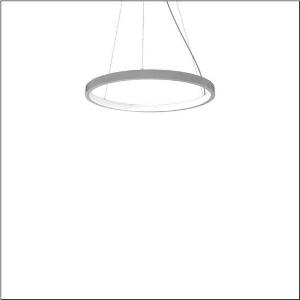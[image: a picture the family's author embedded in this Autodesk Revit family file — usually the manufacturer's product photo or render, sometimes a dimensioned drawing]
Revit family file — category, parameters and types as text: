
# Revit family: silica_r__21_ring-i_5pjbi2d3204a_c88e
name_source: partatom
category: Lighting Fixtures
units: mm (PartAtom-declared; Revit-internal decimal feet)

## family parameters
Cut with Voids When Loaded = No
Host = Face
Light Source = No
Part Type = Normal
Room Calculation Point = No
Round Connector Dimension = Use Diameter
Shared = No

## types (1)
- Silica® 21 Ring-I (1 x LED, 5040 lm, 80 W, 4000K)
    Apparent Load = 80 VA
    CIE Flux Codes = 22 48 76 50 101
    Color Rendering = 80
    Color Temperature = 4000K
    Default Elevation = 1800 mm
    Description = Silica® 21 Ring-I, suspended luminaire, of PMMA, frosted, light emission: inner ring side luminous distribution, primary light characteristic: symmetric, installation type: suspended mounting, LED, rated luminous flux: 5.040lm, luminous efficacy: 63lm/W, light colour: 840, colour temperature: 4000K, with terminal, 5-pole, mains connection: 230V, AC/DC, 0/50..60Hz, rated input power: 80W, housing, of extruded aluminium section, metallic grey (RAL 9006), diameter: 805mm, ceiling canopy, metallic grey (RAL 9006), protection rating (lamp compartment): IP40, insulation class (complete): insulation class I (protective earthing), certification: CE, impact resistance: IK02, permissible operating ambient temperature: 0..+35°C, packaging unit: 1 piece
    Height = 48 mm  [stored 0.15748 ft]
    Lamp = 1 x LED
    Lamp Light Flux = 5040 lm
    Lamp Power = 80 W
    Lamp count = 1
    Length = 805 mm
    Luminous efficacy = 63 lm/W
    Manufacturer = Siteco
    ModVariant = No
    Model = 5PJBI2D3204A
    Mounting Place = Ceiling
    Mounting Type = Pendant
    Number of Poles = 1
    OnlyDefault = Yes
    Power Factor = 1
    Product Name = Silica® 21 Ring-I
    Product group = suspended luminaire
    ProductGroupID = 904
    Protection Class = Protection class I
    Protection Degree = Degree of protection
    RLX_Detail_Level = 1
    RLX_Emergency_Light_Flux = 0 lm
    RLX_Emergency_Type = 0
    RLX_Emergency_Type_DB = No
    RlxData = <blob elided: 13097 chars, md5=f0426e75>
    Socket = socket
    Standby Power = 0 W
    System Light Flux = 5040 lm
    System Power = 80 W
    Type Comments = Product without accessories
    Type Image = l_1251752.jpg
    URL = http://relux.com
    VarID = ---
    Voltage = 0 V
    Weight = 0.00 kg
    Width = 0 mm  [stored 0 ft]

note: [stored X ft] marks values corroborated as IEEE doubles in the binary element streams (Revit-internal decimal feet)

## geometry (parser evidence)
native form markers: Sweep x11
no freeform markers — native parametric forms only
